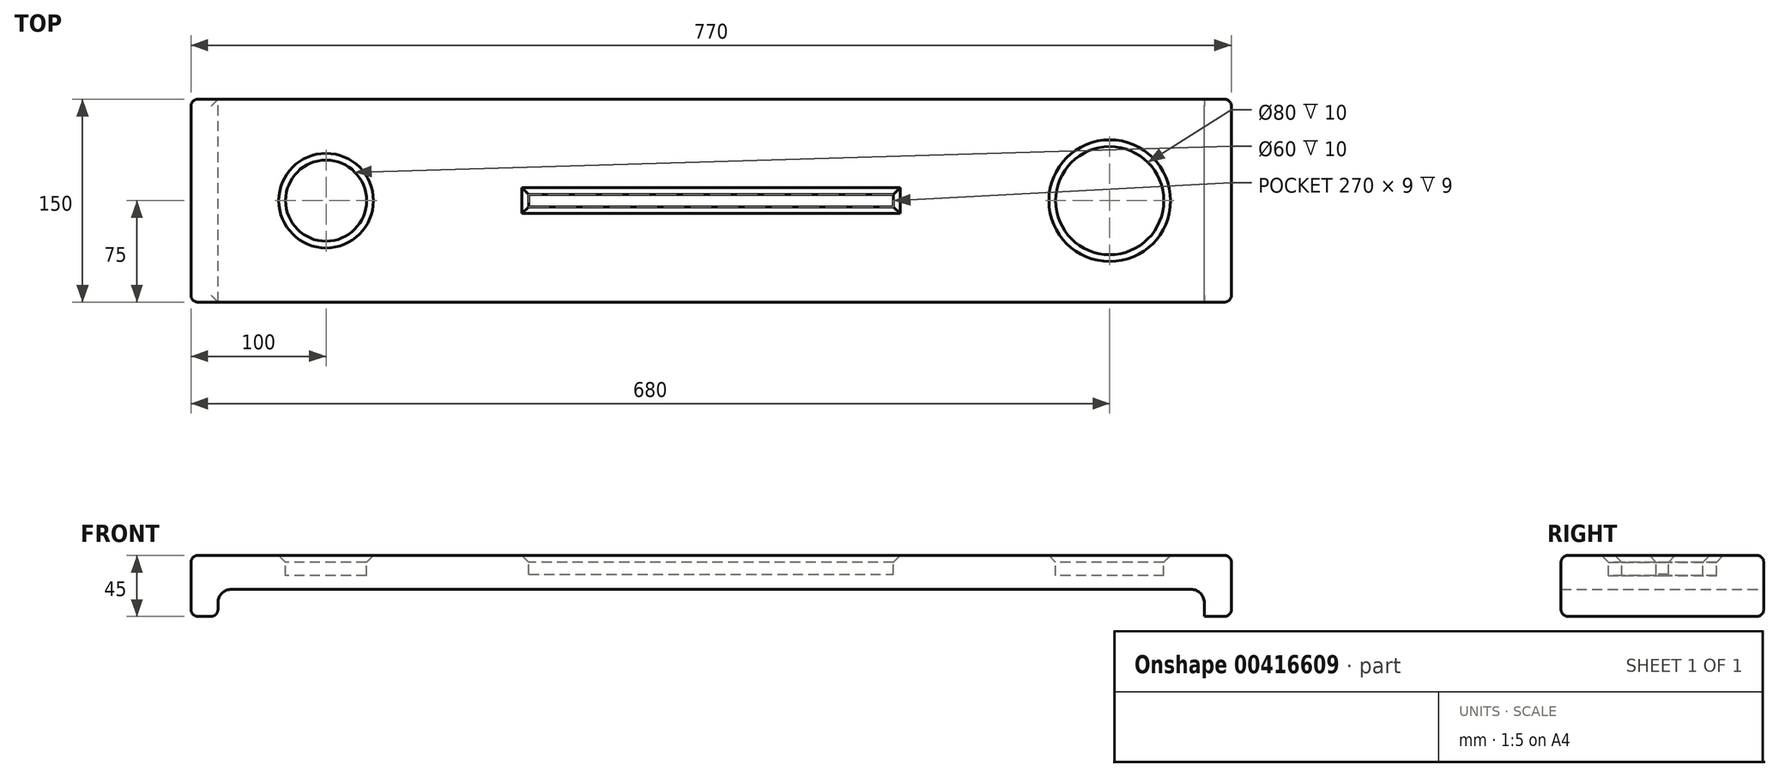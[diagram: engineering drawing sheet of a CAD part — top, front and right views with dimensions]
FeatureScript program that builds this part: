
annotation { "Feature Type Name" : "Feature", "Feature Type Description" : "" }
export const myFeature = defineFeature(function(context is Context, id is Id, definition is map)
    precondition{}
    {
        {
            var Q0;
            Q0=qCreatedBy(makeId("Top.planeOp"),FACE);
            var sketch = newSketch(context, id + "F0", { "sketchPlane" : qUnion([Q0])});
            skLineSegment(sketch, "E0.bottom", {"start": v(0, 0) * mm, "end": v(770, 0) * mm});
            skLineSegment(sketch, "E0.top", {"start": v(0, 150) * mm, "end": v(770, 150) * mm});
            skLineSegment(sketch, "E0.left", {"start": v(0, 0) * mm, "end": v(0, 150) * mm});
            skLineSegment(sketch, "E0.right", {"start": v(770, 0) * mm, "end": v(770, 150) * mm});
            skLineSegment(sketch, "E1", {"start": v(385, 150) * mm, "end": v(385, 0) * mm, "construction": true});
            skSolve(sketch);
        }
        {
            var Q0;
            Q0=makeQuery(id+"F0.imprint","IMPRINT",FACE,{"disambiguationData":[TD([[makeQuery(id+"F0.imprint","IMPRINT",EDGE,{"derivedFrom":sQuery(id+"F0.wireOp",EDGE,"E0.bottom")}),1.0]])]});
            extrude(context, id + "F1", {"entities" : qUnion([Q0]), "depth" : 45 * mm});
        }
        {
            var Q0;
            Q0=makeQuery(id+"F1.opExtrude","CAP_FACE",FACE,{"disambiguationData":[OSD([sQuery(id+"F0.wireOp",EDGE,"E0.bottom"),sQuery(id+"F0.wireOp",EDGE,"E0.top"),sQuery(id+"F0.wireOp",EDGE,"E0.left"),sQuery(id+"F0.wireOp",EDGE,"E0.right")])],"isStart":false});
            var sketch = newSketch(context, id + "F2", { "sketchPlane" : qUnion([Q0])});
            skLineSegment(sketch, "E2.bottom", {"start": v(250, 79.5) * mm, "end": v(520, 79.5) * mm});
            skLineSegment(sketch, "E2.top", {"start": v(250, 70.5) * mm, "end": v(520, 70.5) * mm});
            skLineSegment(sketch, "E2.left", {"start": v(250, 79.5) * mm, "end": v(250, 70.5) * mm});
            skLineSegment(sketch, "E2.right", {"start": v(520, 79.5) * mm, "end": v(520, 70.5) * mm});
            skPoint(sketch, "E2.middle", {"position": v(385, 75) * mm});
            skSolve(sketch);
        }
        {
            var Q0;
            Q0 = qSketchRegion(id + "F2", true);
            extrude(context, id + "F3", {"entities" : qUnion([Q0]), "operationType" : NewBodyOperationType.REMOVE, "oppositeDirection" : true, "depth" : 14 * mm});
        }
        {
            var Q0;
            Q0=makeQuery(id+"F0.imprint","IMPRINT",FACE,{"disambiguationData":[TD([[makeQuery(id+"F0.imprint","IMPRINT",EDGE,{"derivedFrom":sQuery(id+"F0.wireOp",EDGE,"E0.bottom")}),1.0]])]});
            var sketch = newSketch(context, id + "F4", { "sketchPlane" : qUnion([Q0])});
            skLineSegment(sketch, "E3.bottom", {"start": v(20, 0) * mm, "end": v(750, 0) * mm});
            skLineSegment(sketch, "E3.top", {"start": v(20, 150) * mm, "end": v(750, 150) * mm});
            skLineSegment(sketch, "E3.left", {"start": v(20, 0) * mm, "end": v(20, 150) * mm});
            skLineSegment(sketch, "E3.right", {"start": v(750, 0) * mm, "end": v(750, 150) * mm});
            skSolve(sketch);
        }
        {
            var Q0;
            Q0 = qSketchRegion(id + "F4", true);
            extrude(context, id + "F5", {"entities" : qUnion([Q0]), "operationType" : NewBodyOperationType.REMOVE, "depth" : 20 * mm});
        }
        {
            var Q0;
            Q0=makeQuery(id+"F2.imprint","IMPRINT",FACE,{"disambiguationData":[TD([[makeQuery(id+"F2.imprint","IMPRINT",EDGE,{"derivedFrom":sQuery(id+"F2.wireOp",EDGE,"E2.bottom")}),1.0]])]});
            var sketch = newSketch(context, id + "F6", { "sketchPlane" : qUnion([Q0])});
            skCircle(sketch, "E4", {"center": v(680, 75) * mm, "radius": 40 * mm});
            skSolve(sketch);
        }
        {
            var Q0;
            Q0 = qSketchRegion(id + "F6", true);
            extrude(context, id + "F7", {"entities" : qUnion([Q0]), "operationType" : NewBodyOperationType.REMOVE, "oppositeDirection" : true, "depth" : 15 * mm});
        }
        {
            var Q0;
            Q0=makeQuery(id+"F2.imprint","IMPRINT",FACE,{"disambiguationData":[TD([[makeQuery(id+"F2.imprint","IMPRINT",EDGE,{"derivedFrom":sQuery(id+"F2.wireOp",EDGE,"E2.bottom")}),1.0]])]});
            var sketch = newSketch(context, id + "F8", { "sketchPlane" : qUnion([Q0])});
            skCircle(sketch, "E5", {"center": v(100, 75) * mm, "radius": 30 * mm});
            skSolve(sketch);
        }
        {
            var Q0;
            Q0 = qSketchRegion(id + "F8", true);
            extrude(context, id + "F9", {"entities" : qUnion([Q0]), "operationType" : NewBodyOperationType.REMOVE, "oppositeDirection" : true, "depth" : 15 * mm});
        }
        {
            var Q0;
            Q0=makeQuery(id+"F1.opExtrude","SWEPT_EDGE",EDGE,{"disambiguationData":[OSD([sQuery(id+"F0.wireOp",EDGE,"E0.bottom"),sQuery(id+"F0.wireOp",EDGE,"E0.right")])]});
            var Q1;
            Q1=makeQuery(id+"F1.opExtrude","SWEPT_EDGE",EDGE,{"disambiguationData":[OSD([sQuery(id+"F0.wireOp",EDGE,"E0.top"),sQuery(id+"F0.wireOp",EDGE,"E0.right")])]});
            var Q2;
            Q2=makeQuery(id+"F1.opExtrude","CAP_EDGE",EDGE,{"disambiguationData":[OSD([sQuery(id+"F0.wireOp",EDGE,"E0.right")])],"isStart":false});
            var Q3;
            Q3=makeQuery(id+"F1.opExtrude","CAP_EDGE",EDGE,{"disambiguationData":[OSD([sQuery(id+"F0.wireOp",EDGE,"E0.bottom")])],"isStart":false});
            var Q4;
            Q4=makeQuery(id+"F1.opExtrude","CAP_EDGE",EDGE,{"disambiguationData":[OSD([sQuery(id+"F0.wireOp",EDGE,"E0.top")])],"isStart":false});
            var Q5;
            Q5=makeQuery(id+"F1.opExtrude","CAP_EDGE",EDGE,{"disambiguationData":[OSD([sQuery(id+"F0.wireOp",EDGE,"E0.left")])],"isStart":false});
            var Q6;
            Q6=makeQuery(id+"F5.boolean.opBoolean","COPY",EDGE,{"derivedFrom":makeQuery(id+"F5.opExtrude","CAP_EDGE",EDGE,{"disambiguationData":[OSD([sQuery(id+"F4.wireOp",EDGE,"E3.top")])],"isStart":false})});
            var Q7;
            Q7=makeQuery(id+"F1.opExtrude","CAP_EDGE",EDGE,{"disambiguationData":[OSD([sQuery(id+"F0.wireOp",EDGE,"E0.right")])],"isStart":true});
            var Q8;
            Q8=makeQuery(id+"F5.boolean.opBoolean","COPY",EDGE,{"derivedFrom":makeQuery(id+"F5.opExtrude","SWEPT_EDGE",EDGE,{"disambiguationData":[OSD([sQuery(id+"F0.wireOp",EDGE,"E0.bottom"),sQuery(id+"F4.wireOp",EDGE,"E3.bottom"),sQuery(id+"F4.wireOp",EDGE,"E3.right")])]})});
            var Q9;
            {var subQ0=sQuery(id+"F0.wireOp",EDGE,"E0.bottom");var subQ1=sQuery(id+"F0.wireOp",EDGE,"E0.right");Q9=makeQuery(id+"F5.boolean.opBoolean","SPLIT",EDGE,{"disambiguationData":[TD([makeQuery(id+"F1.opExtrude","SWEPT_FACE",FACE,{"disambiguationData":[OSD([subQ1])]})])],"derivedFrom":makeQuery(id+"F1.opExtrude","CAP_EDGE",EDGE,{"disambiguationData":[OSD([subQ0])],"isStart":true})});}
            var Q10;
            Q10=makeQuery(id+"F5.boolean.opBoolean","COPY",EDGE,{"derivedFrom":makeQuery(id+"F5.opExtrude","CAP_EDGE",EDGE,{"disambiguationData":[OSD([sQuery(id+"F4.wireOp",EDGE,"E3.bottom")])],"isStart":false})});
            var Q11;
            Q11=makeQuery(id+"F5.boolean.opBoolean","COPY",EDGE,{"derivedFrom":makeQuery(id+"F5.opExtrude","CAP_EDGE",EDGE,{"disambiguationData":[OSD([sQuery(id+"F4.wireOp",EDGE,"E3.left")])],"isStart":true})});
            var Q12;
            Q12=makeQuery(id+"F5.boolean.opBoolean","COPY",EDGE,{"derivedFrom":makeQuery(id+"F5.opExtrude","SWEPT_EDGE",EDGE,{"disambiguationData":[OSD([sQuery(id+"F0.wireOp",EDGE,"E0.bottom"),sQuery(id+"F4.wireOp",EDGE,"E3.bottom"),sQuery(id+"F4.wireOp",EDGE,"E3.left")])]})});
            var Q13;
            Q13=makeQuery(id+"F1.opExtrude","SWEPT_EDGE",EDGE,{"disambiguationData":[OSD([sQuery(id+"F0.wireOp",EDGE,"E0.bottom"),sQuery(id+"F0.wireOp",EDGE,"E0.left")])]});
            var Q14;
            Q14=makeQuery(id+"F1.opExtrude","SWEPT_EDGE",EDGE,{"disambiguationData":[OSD([sQuery(id+"F0.wireOp",EDGE,"E0.top"),sQuery(id+"F0.wireOp",EDGE,"E0.left")])]});
            var Q15;
            Q15=makeQuery(id+"F5.boolean.opBoolean","COPY",EDGE,{"derivedFrom":makeQuery(id+"F5.opExtrude","SWEPT_EDGE",EDGE,{"disambiguationData":[OSD([sQuery(id+"F0.wireOp",EDGE,"E0.top"),sQuery(id+"F4.wireOp",EDGE,"E3.top"),sQuery(id+"F4.wireOp",EDGE,"E3.left")])]})});
            var Q16;
            {var subQ0=sQuery(id+"F0.wireOp",EDGE,"E0.left");var subQ1=sQuery(id+"F0.wireOp",EDGE,"E0.top");Q16=makeQuery(id+"F5.boolean.opBoolean","SPLIT",EDGE,{"disambiguationData":[TD([makeQuery(id+"F1.opExtrude","SWEPT_FACE",FACE,{"disambiguationData":[OSD([subQ0])]})])],"derivedFrom":makeQuery(id+"F1.opExtrude","CAP_EDGE",EDGE,{"disambiguationData":[OSD([subQ1])],"isStart":true})});}
            var Q17;
            Q17=makeQuery(id+"F1.opExtrude","CAP_EDGE",EDGE,{"disambiguationData":[OSD([sQuery(id+"F0.wireOp",EDGE,"E0.left")])],"isStart":true});
            var Q18;
            Q18=makeQuery(id+"F5.boolean.opBoolean","COPY",EDGE,{"derivedFrom":makeQuery(id+"F5.opExtrude","SWEPT_EDGE",EDGE,{"disambiguationData":[OSD([sQuery(id+"F0.wireOp",EDGE,"E0.top"),sQuery(id+"F4.wireOp",EDGE,"E3.top"),sQuery(id+"F4.wireOp",EDGE,"E3.right")])]})});
            var Q19;
            Q19=makeQuery(id+"F5.boolean.opBoolean","COPY",EDGE,{"derivedFrom":makeQuery(id+"F5.opExtrude","CAP_EDGE",EDGE,{"disambiguationData":[OSD([sQuery(id+"F4.wireOp",EDGE,"E3.right")])],"isStart":true})});
            var Q20;
            {var subQ0=sQuery(id+"F0.wireOp",EDGE,"E0.right");var subQ1=sQuery(id+"F0.wireOp",EDGE,"E0.top");Q20=makeQuery(id+"F5.boolean.opBoolean","SPLIT",EDGE,{"disambiguationData":[TD([makeQuery(id+"F1.opExtrude","SWEPT_FACE",FACE,{"disambiguationData":[OSD([subQ0])]})])],"derivedFrom":makeQuery(id+"F1.opExtrude","CAP_EDGE",EDGE,{"disambiguationData":[OSD([subQ1])],"isStart":true})});}
            var Q21;
            {var subQ0=sQuery(id+"F0.wireOp",EDGE,"E0.bottom");var subQ1=sQuery(id+"F0.wireOp",EDGE,"E0.left");Q21=makeQuery(id+"F5.boolean.opBoolean","SPLIT",EDGE,{"disambiguationData":[TD([makeQuery(id+"F1.opExtrude","SWEPT_FACE",FACE,{"disambiguationData":[OSD([subQ1])]})])],"derivedFrom":makeQuery(id+"F1.opExtrude","CAP_EDGE",EDGE,{"disambiguationData":[OSD([subQ0])],"isStart":true})});}
            fillet(context, id + "F10", {"entities" : qUnion([Q0, Q1, Q2, Q3, Q4, Q5, Q6, Q7, Q8, Q9, Q10, Q11, Q12, Q13, Q14, Q15, Q16, Q17, Q18, Q19, Q20, Q21]), "radius" : 5 * mm, "tangentPropagation" : true, "allowEdgeOverflow" : false});
        }
        {
            var Q0;
            Q0=makeQuery(id+"F5.boolean.opBoolean","COPY",EDGE,{"derivedFrom":makeQuery(id+"F5.opExtrude","CAP_EDGE",EDGE,{"disambiguationData":[OSD([sQuery(id+"F4.wireOp",EDGE,"E3.left")])],"isStart":false})});
            var Q1;
            Q1=makeQuery(id+"F5.boolean.opBoolean","COPY",EDGE,{"derivedFrom":makeQuery(id+"F5.opExtrude","CAP_EDGE",EDGE,{"disambiguationData":[OSD([sQuery(id+"F4.wireOp",EDGE,"E3.right")])],"isStart":false})});
            fillet(context, id + "F11", {"entities" : qUnion([Q0, Q1]), "radius" : 10 * mm, "tangentPropagation" : true, "allowEdgeOverflow" : false});
        }
        {
            var Q0;
            Q0=makeQuery(id+"F9.boolean.opBoolean","COPY",EDGE,{"derivedFrom":makeQuery(id+"F9.opExtrude","CAP_EDGE",EDGE,{"disambiguationData":[OSD([sQuery(id+"F8.wireOp",EDGE,"E5")])],"isStart":true})});
            var Q1;
            Q1=makeQuery(id+"F3.boolean.opBoolean","COPY",EDGE,{"derivedFrom":makeQuery(id+"F3.opExtrude","CAP_EDGE",EDGE,{"disambiguationData":[OSD([sQuery(id+"F2.wireOp",EDGE,"E2.top")])],"isStart":true})});
            var Q2;
            Q2=makeQuery(id+"F3.boolean.opBoolean","COPY",EDGE,{"derivedFrom":makeQuery(id+"F3.opExtrude","CAP_EDGE",EDGE,{"disambiguationData":[OSD([sQuery(id+"F2.wireOp",EDGE,"E2.left")])],"isStart":true})});
            var Q3;
            Q3=makeQuery(id+"F3.boolean.opBoolean","COPY",EDGE,{"derivedFrom":makeQuery(id+"F3.opExtrude","CAP_EDGE",EDGE,{"disambiguationData":[OSD([sQuery(id+"F2.wireOp",EDGE,"E2.bottom")])],"isStart":true})});
            var Q4;
            Q4=makeQuery(id+"F3.boolean.opBoolean","COPY",EDGE,{"derivedFrom":makeQuery(id+"F3.opExtrude","CAP_EDGE",EDGE,{"disambiguationData":[OSD([sQuery(id+"F2.wireOp",EDGE,"E2.right")])],"isStart":true})});
            var Q5;
            Q5=makeQuery(id+"F1.opExtrude","CAP_FACE",FACE,{"disambiguationData":[OSD([sQuery(id+"F0.wireOp",EDGE,"E0.bottom"),sQuery(id+"F0.wireOp",EDGE,"E0.top"),sQuery(id+"F0.wireOp",EDGE,"E0.left"),sQuery(id+"F0.wireOp",EDGE,"E0.right")])],"isStart":false});
            chamfer(context, id + "F12", {"entities" : qUnion([Q0, Q1, Q2, Q3, Q4, Q5]), "width" : 5 * mm, "tangentPropagation" : true});
        }
    });
